# Revit family: TV121-1.9_RFA
name_source: partatom
category: Aparatos sanitarios
units: mm (PartAtom-declared; Revit-internal decimal feet)

## family parameters
Compartido = No
Corte con vacíos al cargar = No
Cota de conector redondo = Diámetro de uso
Número OmniClass = 23.45.00.00
Punto de cálculo de habitación = No
Se basa en plano de trabajo = No
Siempre vertical = Sí
Tipo de pieza = Normal
Título OmniClass = Sanitary, Laundry, and Cleaning Equipment

## types (1)
- TV121-1.9
    Certification = http://www.helvex.com.mx
    Chrome = Brass Chromed
    Comentarios de tipo = Special Products
    Conexión AF = No
    Connection = ½" - 14 NPSM
    Descripción = Single Faucet Economizer To Wall Closing And Antibacterial Coating
    Documentation = http://www.helvex.com.mx
    Elevación por defecto = 0"
    Fabricante = HELVEX
    Features = Automatic Closure, Activation Time Adjustable, Button With Antibacterial Coating, Closing Time Adjustable From 5 To 13 Seconds
    Instructive = http://www.helvex.com.mx
    Max. Water Flow = 2.1 gal/min
    Max. Working Pressure = 85.3 psi
    Min. Working Pressure = 14.2 psi
    Modelo = TV121-1.9
    Support Base Diameter = 2"
    Total Length = 8"
    URL = http://www.helvex.com.mx

## geometry (parser evidence)
native form markers: Sweep x3
no freeform markers — native parametric forms only
